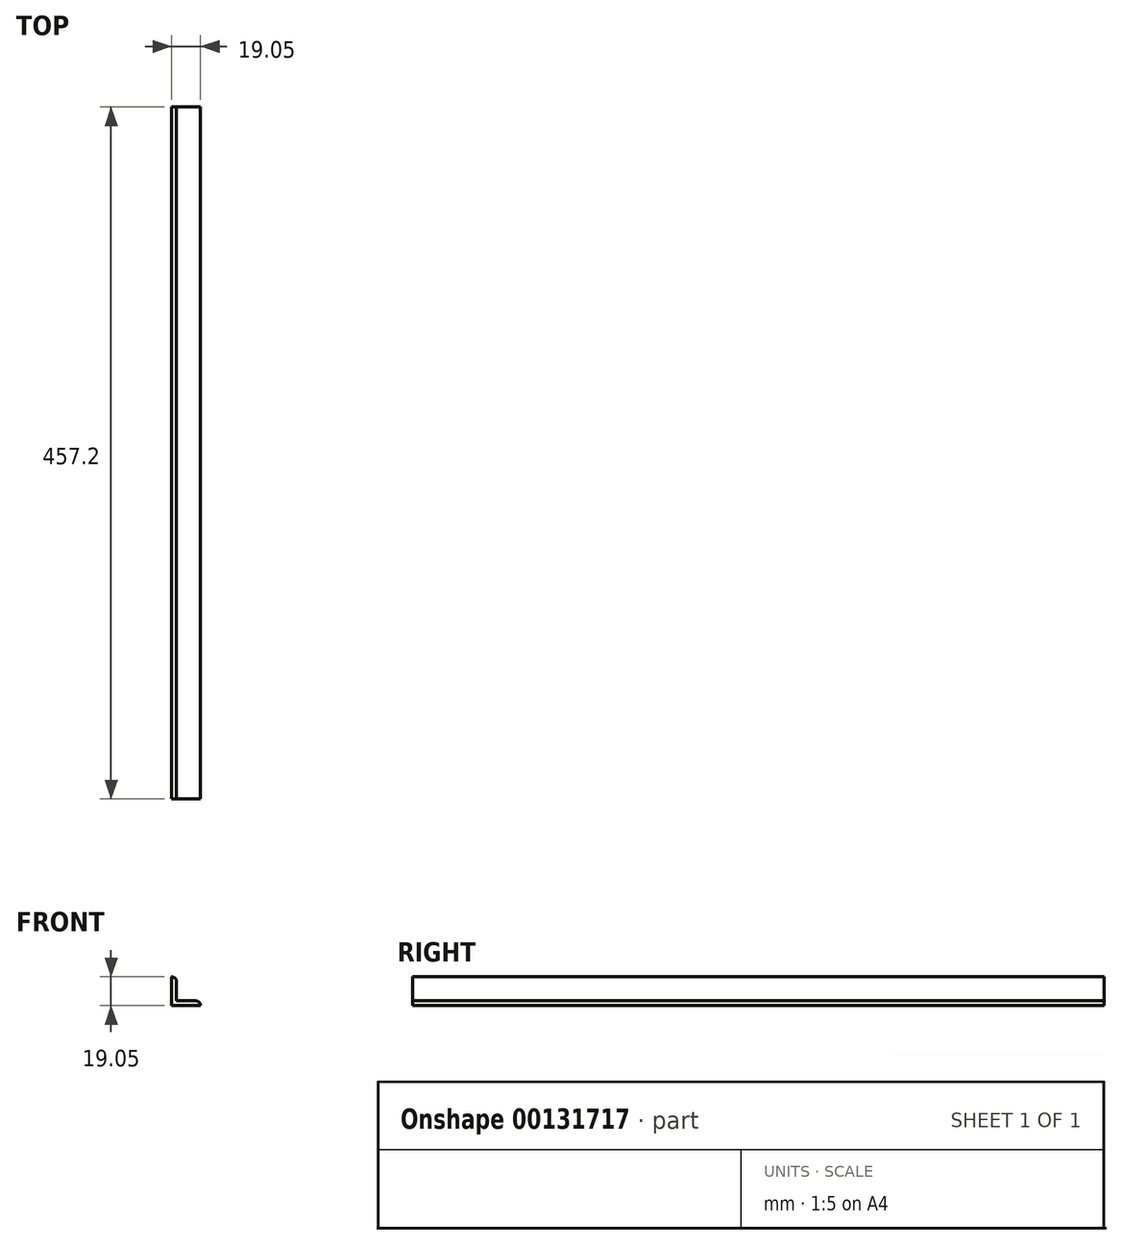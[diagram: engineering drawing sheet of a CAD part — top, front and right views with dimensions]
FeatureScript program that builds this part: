
annotation { "Feature Type Name" : "Feature", "Feature Type Description" : "" }
export const myFeature = defineFeature(function(context is Context, id is Id, definition is map)
    precondition{}
    {
        {
            var Q0;
            Q0=qCreatedBy(makeId("Front.planeOp"),FACE);
            var sketch = newSketch(context, id + "F0", { "sketchPlane" : qUnion([Q0])});
            skLineSegment(sketch, "E0", {"start": v(0, 19.05) * mm, "end": v(0, 0) * mm});
            skLineSegment(sketch, "E1", {"start": v(0, 0) * mm, "end": v(19.05, 0) * mm});
            skLineSegment(sketch, "E2", {"start": v(15.88, 3.17) * mm, "end": v(3.18, 3.17) * mm});
            skLineSegment(sketch, "E3", {"start": v(3.17, 3.17) * mm, "end": v(3.17, 15.88) * mm});
            skLineSegment(sketch, "E4", {"start": v(0, 19.05) * mm, "end": v(0, 19.05) * mm});
            skArc(sketch, "E5.filletArc", {"start": v(3.17, 15.88) * mm, "mid": v(2.25, 18.12) * mm, "end": v(0, 19.05) * mm});
            skArc(sketch, "E6.filletArc", {"start": v(19.05, 0) * mm, "mid": v(18.12, 2.25) * mm, "end": v(15.88, 3.18) * mm});
            skSolve(sketch);
        }
        {
            var Q0;
            Q0=makeQuery(id+"F0.imprint","IMPRINT",FACE,{"disambiguationData":[TD([[makeQuery(id+"F0.imprint","IMPRINT",EDGE,{"derivedFrom":sQuery(id+"F0.wireOp",EDGE,"E0")}),1.0]])]});
            extrude(context, id + "F1", {"entities" : qUnion([Q0]), "endBound" : BoundingType.SYMMETRIC, "depth" : 457.2 * mm});
        }
    });
